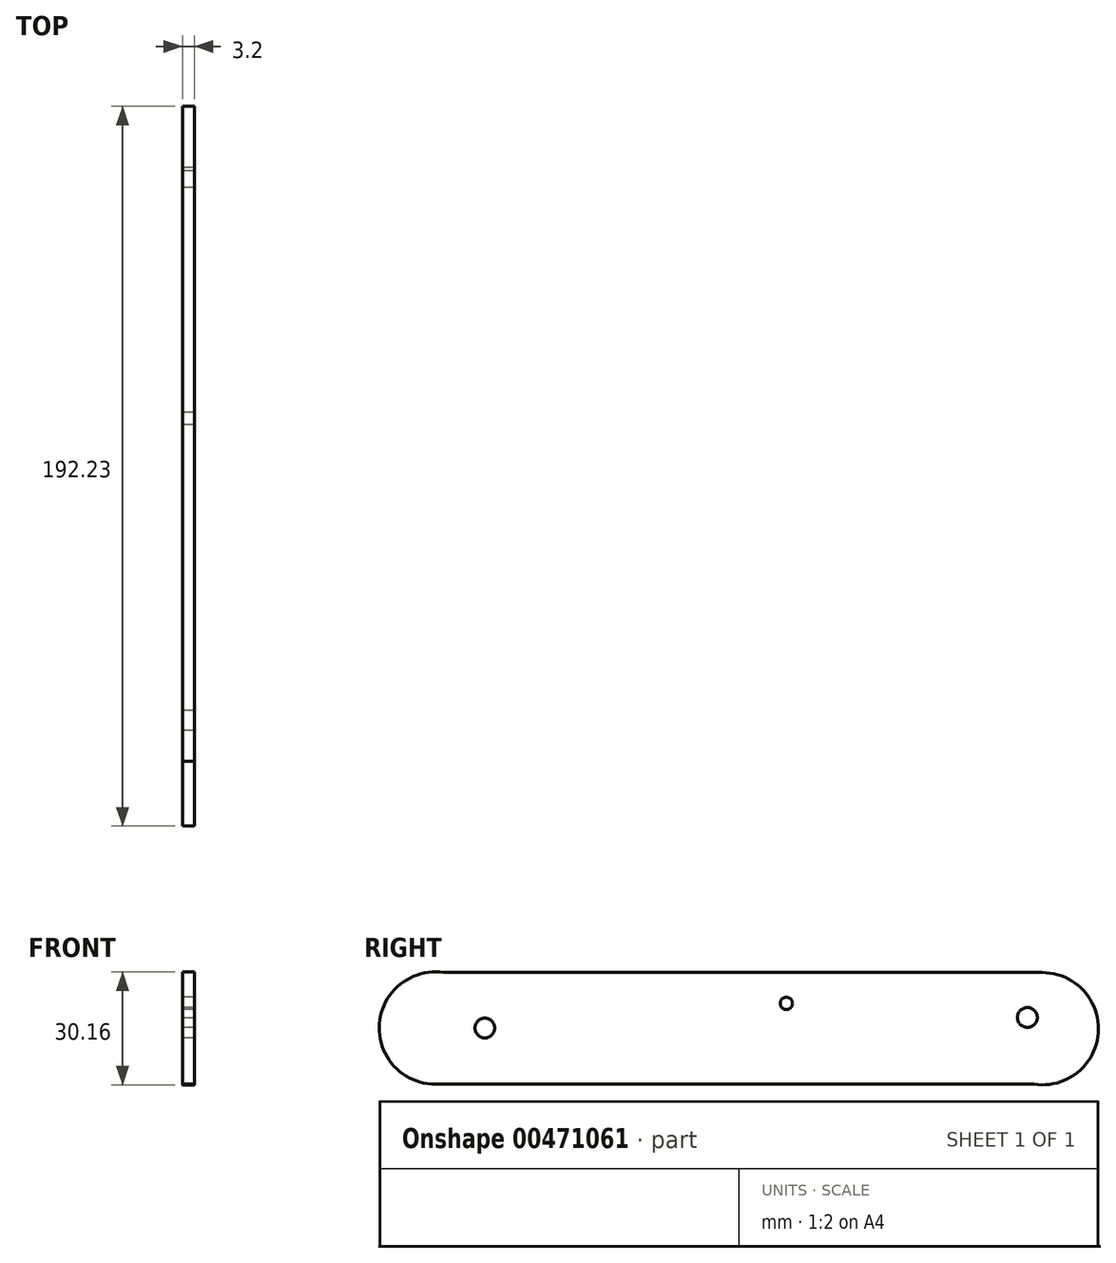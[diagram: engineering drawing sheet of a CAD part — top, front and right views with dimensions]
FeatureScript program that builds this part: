
annotation { "Feature Type Name" : "Feature", "Feature Type Description" : "" }
export const myFeature = defineFeature(function(context is Context, id is Id, definition is map)
    precondition{}
    {
        {
            var Q0;
            Q0=qCreatedBy(makeId("Right.planeOp"),FACE);
            var sketch = newSketch(context, id + "F0", { "sketchPlane" : qUnion([Q0])});
            skCircle(sketch, "E0", {"center": v(-84.06, 9.6) * mm, "radius": 2.65 * mm});
            skLineSegment(sketch, "E1", {"start": v(-95.06, 24.44) * mm, "end": v(64.94, 24.44) * mm});
            skLineSegment(sketch, "E2", {"start": v(-97.29, -5.4) * mm, "end": v(62.71, -5.4) * mm});
            skCircle(sketch, "E3", {"center": v(60.94, 12.44) * mm, "radius": 2.65 * mm});
            skArc(sketch, "E4", {"start": v(-95.06, 24.44) * mm, "mid": v(-112.25, 10.72) * mm, "end": v(-97.29, -5.4) * mm});
            skArc(sketch, "E5", {"start": v(62.71, -5.4) * mm, "mid": v(79.9, 8.32) * mm, "end": v(64.94, 24.44) * mm});
            skCircle(sketch, "E6", {"center": v(-3.48, 16.2) * mm, "radius": 1.65 * mm});
            skSolve(sketch);
        }
        {
            var Q0;
            Q0 = qSketchRegion(id + "F0", true);
            extrude(context, id + "F1", {"entities" : qUnion([Q0]), "depth" : 3.2 * mm, "offsetDistance" : 25 * mm});
        }
    });
